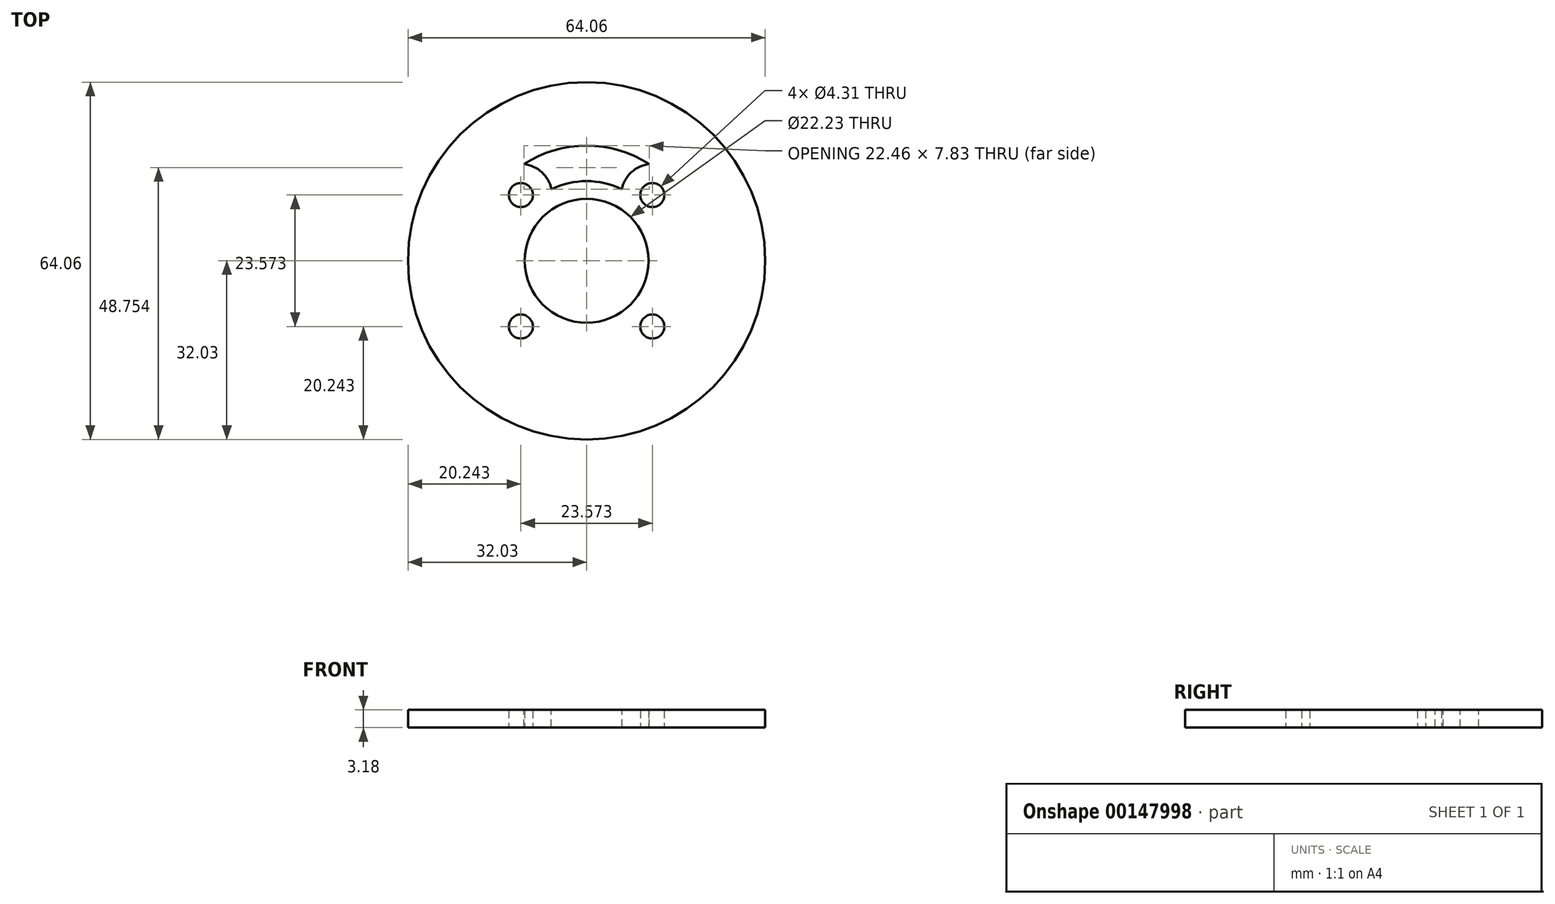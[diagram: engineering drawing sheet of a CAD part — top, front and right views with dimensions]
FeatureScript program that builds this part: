
annotation { "Feature Type Name" : "Feature", "Feature Type Description" : "" }
export const myFeature = defineFeature(function(context is Context, id is Id, definition is map)
    precondition{}
    {
        {
            var Q0;
            Q0=qCreatedBy(makeId("Top.planeOp"),FACE);
            var sketch = newSketch(context, id + "F0", { "sketchPlane" : qUnion([Q0])});
            skCircle(sketch, "E0", {"center": v(0, 0) * mm, "radius": 11.11 * mm});
            skLineSegment(sketch, "E1.bottom", {"start": v(11.79, -11.79) * mm, "end": v(-11.79, -11.79) * mm, "construction": true});
            skLineSegment(sketch, "E1.top", {"start": v(11.79, 11.79) * mm, "end": v(-11.79, 11.79) * mm, "construction": true});
            skLineSegment(sketch, "E1.left", {"start": v(11.79, -11.79) * mm, "end": v(11.79, 11.79) * mm, "construction": true});
            skLineSegment(sketch, "E1.right", {"start": v(-11.79, -11.79) * mm, "end": v(-11.79, 11.79) * mm, "construction": true});
            skCircle(sketch, "E2", {"center": v(-11.79, 11.79) * mm, "radius": 5.56 * mm, "construction": true});
            skCircle(sketch, "E3", {"center": v(-11.79, 11.79) * mm, "radius": 2.15 * mm});
            skCircle(sketch, "E4", {"center": v(11.79, 11.79) * mm, "radius": 2.15 * mm});
            skCircle(sketch, "E5", {"center": v(11.79, -11.79) * mm, "radius": 2.15 * mm});
            skCircle(sketch, "E6", {"center": v(-11.79, -11.79) * mm, "radius": 2.15 * mm});
            skCircle(sketch, "E7", {"center": v(0, 0) * mm, "radius": 32.03 * mm});
            skSolve(sketch);
        }
        {
            var Q0;
            Q0=qSketchRegion(id+"F0",true);
            extrude(context, id + "F1", {"entities" : qUnion([Q0]), "depth" : 3.17 * mm});
        }
        {
            var Q0;
            Q0=makeQuery(id+"F1.opExtrude","CAP_FACE",FACE,{"disambiguationData":[OSD([sQuery(id+"F0.wireOp",EDGE,"E0"),sQuery(id+"F0.wireOp",EDGE,"E3"),sQuery(id+"F0.wireOp",EDGE,"E4"),sQuery(id+"F0.wireOp",EDGE,"E5"),sQuery(id+"F0.wireOp",EDGE,"E6"),sQuery(id+"F0.wireOp",EDGE,"E7")])],"isStart":false});
            var sketch = newSketch(context, id + "F2", { "sketchPlane" : qUnion([Q0])});
            skArc(sketch, "E8", {"start": v(-6.33, 12.81) * mm, "mid": v(-8.03, 15.88) * mm, "end": v(-11.23, 17.31) * mm});
            skArc(sketch, "E9", {"start": v(6.33, 12.81) * mm, "mid": v(0, 14.29) * mm, "end": v(-6.33, 12.81) * mm});
            skArc(sketch, "E10", {"start": v(11.23, 17.31) * mm, "mid": v(8.03, 15.88) * mm, "end": v(6.33, 12.81) * mm});
            skArc(sketch, "E11", {"start": v(11.23, 17.31) * mm, "mid": v(0, 20.64) * mm, "end": v(-11.23, 17.31) * mm});
            skSolve(sketch);
        }
        {
            var Q0;
            Q0=qSketchRegion(id+"F2",true);
            var Q1;
            Q1=makeQuery(id+"F1.opExtrude","CAP_FACE",FACE,{"disambiguationData":[OSD([sQuery(id+"F0.wireOp",EDGE,"E0"),sQuery(id+"F0.wireOp",EDGE,"E3"),sQuery(id+"F0.wireOp",EDGE,"E4"),sQuery(id+"F0.wireOp",EDGE,"E5"),sQuery(id+"F0.wireOp",EDGE,"E6"),sQuery(id+"F0.wireOp",EDGE,"E7")])],"isStart":true});
            extrude(context, id + "F3", {"entities" : qUnion([Q0]), "operationType" : NewBodyOperationType.REMOVE, "endBound" : BoundingType.UP_TO_SURFACE, "oppositeDirection" : true, "endBoundEntityFace" : qUnion([Q1]), "depth" : 25.4 * mm});
        }
    });
